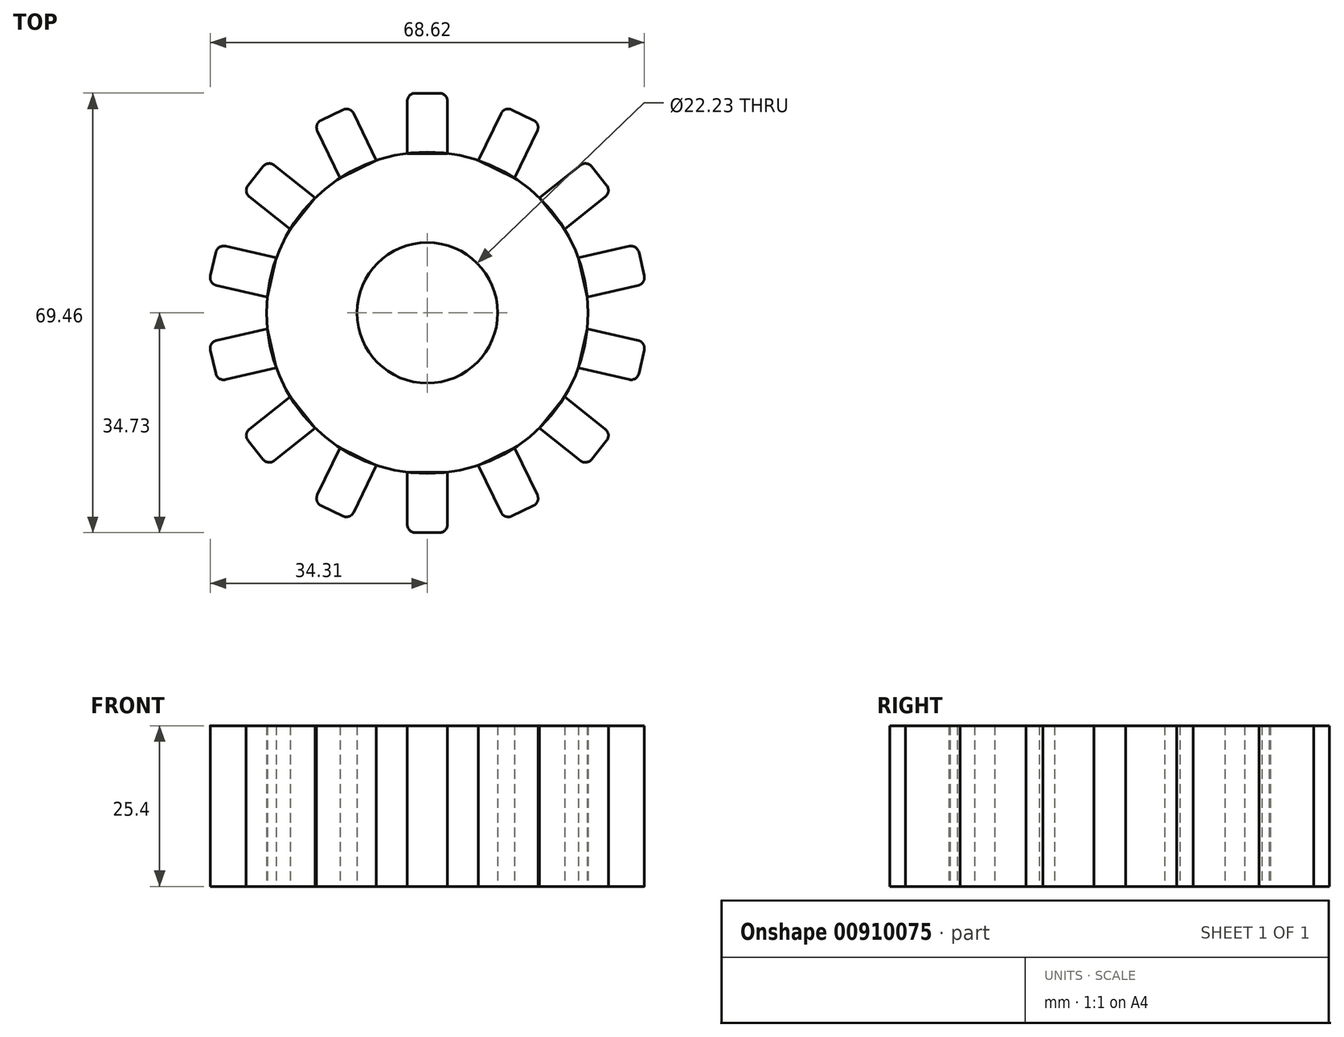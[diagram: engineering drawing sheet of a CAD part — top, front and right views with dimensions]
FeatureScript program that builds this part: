
annotation { "Feature Type Name" : "Feature", "Feature Type Description" : "" }
export const myFeature = defineFeature(function(context is Context, id is Id, definition is map)
    precondition{}
    {
        {
            var Q0;
            Q0=qCreatedBy(makeId("Top.planeOp"),FACE);
            var sketch = newSketch(context, id + "F0", { "sketchPlane" : qUnion([Q0])});
            skCircle(sketch, "E0", {"center": v(0, 0) * mm, "radius": 25.4 * mm});
            skCircle(sketch, "E1", {"center": v(0, 0) * mm, "radius": 11.11 * mm});
            skSolve(sketch);
        }
        {
            var Q0;
            Q0=qCreatedBy(makeId("Top.planeOp"),FACE);
            var sketch = newSketch(context, id + "F1", { "sketchPlane" : qUnion([Q0])});
            skLineSegment(sketch, "E2", {"start": v(-3.17, 25.2) * mm, "end": v(3.17, 25.2) * mm});
            skLineSegment(sketch, "E3", {"start": v(3.17, 25.2) * mm, "end": v(3.17, 33.46) * mm});
            skLineSegment(sketch, "E4", {"start": v(1.9, 34.73) * mm, "end": v(-1.9, 34.73) * mm});
            skLineSegment(sketch, "E5", {"start": v(-3.18, 33.46) * mm, "end": v(-3.18, 25.2) * mm});
            skPoint(sketch, "E6.visualSharp", {"position": v(-3.18, 34.73) * mm});
            skArc(sketch, "E6.filletArc", {"start": v(-1.9, 34.73) * mm, "mid": v(-2.8, 34.35) * mm, "end": v(-3.18, 33.46) * mm});
            skPoint(sketch, "E7.visualSharp", {"position": v(3.17, 34.73) * mm});
            skArc(sketch, "E7.filletArc", {"start": v(3.17, 33.46) * mm, "mid": v(2.8, 34.35) * mm, "end": v(1.9, 34.73) * mm});
            skSolve(sketch);
        }
        {
            var Q0;
            Q0 = qSketchRegion(id + "F0", true);
            var Q1;
            Q1 = qSketchRegion(id + "F1", true);
            extrude(context, id + "F2", {"entities" : qUnion([Q0, Q1]), "depth" : 25.4 * mm, "offsetDistance" : 25.4 * mm});
        }
        {
            var Q0;
            Q0=makeQuery(id+"F2.opExtrude","SWEPT_BODY",BODY,{"disambiguationData":[OSD([sQuery(id+"F1.wireOp",EDGE,"E2"),sQuery(id+"F1.wireOp",EDGE,"E3"),sQuery(id+"F1.wireOp",EDGE,"E4"),sQuery(id+"F1.wireOp",EDGE,"E5"),sQuery(id+"F1.wireOp",EDGE,"E6.filletArc"),sQuery(id+"F1.wireOp",EDGE,"E7.filletArc")])]});
            var Q1;
            Q1=makeQuery(id+"F2.opExtrude","SWEPT_FACE",FACE,{"disambiguationData":[OSD([sQuery(id+"F0.wireOp",EDGE,"E0")])]});
            circularPattern(context, id + "F3", {"entities" : qUnion([Q0]), "axis" : qUnion([Q1]), "angle" : 360 * degree, "instanceCount" : 14, "equalSpace" : true});
        }
    });
